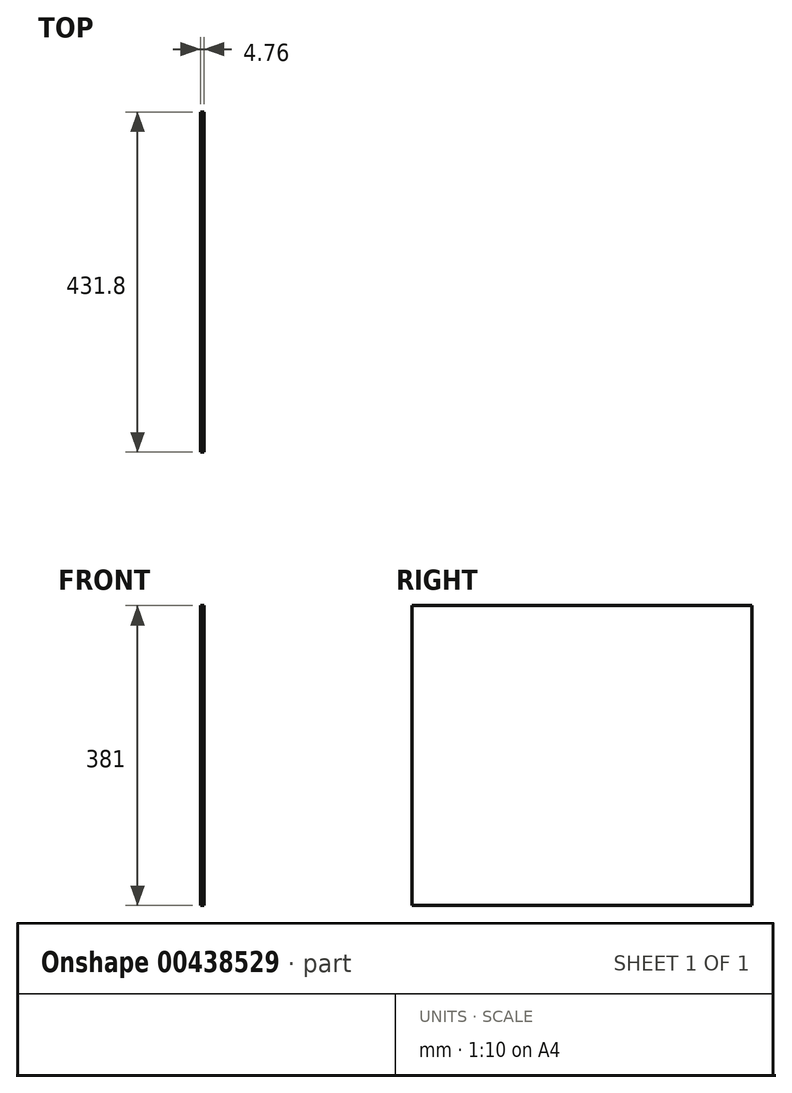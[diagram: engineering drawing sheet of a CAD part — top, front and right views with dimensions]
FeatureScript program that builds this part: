
annotation { "Feature Type Name" : "Feature", "Feature Type Description" : "" }
export const myFeature = defineFeature(function(context is Context, id is Id, definition is map)
    precondition{}
    {
        {
            var Q0;
            Q0=qCreatedBy(makeId("Right.planeOp"),FACE);
            var sketch = newSketch(context, id + "F0", { "sketchPlane" : qUnion([Q0])});
            skLineSegment(sketch, "E0.bottom", {"start": v(-236.29, 196.66) * mm, "end": v(195.51, 196.66) * mm});
            skLineSegment(sketch, "E0.top", {"start": v(-236.29, -184.34) * mm, "end": v(195.51, -184.34) * mm});
            skLineSegment(sketch, "E0.left", {"start": v(-236.29, 196.66) * mm, "end": v(-236.29, -184.34) * mm});
            skLineSegment(sketch, "E0.right", {"start": v(195.51, 196.66) * mm, "end": v(195.51, -184.34) * mm});
            skSolve(sketch);
        }
        {
            var Q0;
            Q0=makeQuery(id+"F0.imprint","IMPRINT",FACE,{"disambiguationData":[TD([[makeQuery(id+"F0.imprint","IMPRINT",EDGE,{"derivedFrom":sQuery(id+"F0.wireOp",EDGE,"E0.bottom")}),-1.0]])]});
            extrude(context, id + "F1", {"entities" : qUnion([Q0]), "depth" : 4.76 * mm});
        }
    });
